# Revit family: F155-38x38x32
name_source: partatom
category: Furniture Systems
units: mm (PartAtom-declared; Revit-internal decimal feet)

## family parameters
Always vertical = Yes
Cut with Voids When Loaded = No
Part Type = Normal
Room Calculation Point = No
Round Connector Dimension = Use Diameter
Shared = No
Work Plane-Based = No

## types (2) — shared parameters
Base = <By Category>
Description = Bubble Two Step Inside Corner, 38Lx38Wx32H
Glide Frame = Glide
Low Profile = Black
Manufacturer = Fomcore
Product = https://fomcore.com
Side Fabric = <By Category>
Step-1 Fabric = <By Category>
Step-2 Fabric = <By Category>
Type Comments = Step Series
URL = https://fomcore.com
zero-valued in all types: Cost

## per-type parameters (varying)
| type | G1 | Glide | L1 | LEG OPTIONS | Leg H |
| F154-38x38x32-G1 | Yes | Black | No | 1 | 3/4" |
| F154-38x38x32-L1 | No | <By Category> | Yes | 2 | 1" |

note: column(s) folded — value = type name in every type: Model

## geometry (parser evidence)
native form markers: Sweep x8
no freeform markers — native parametric forms only
